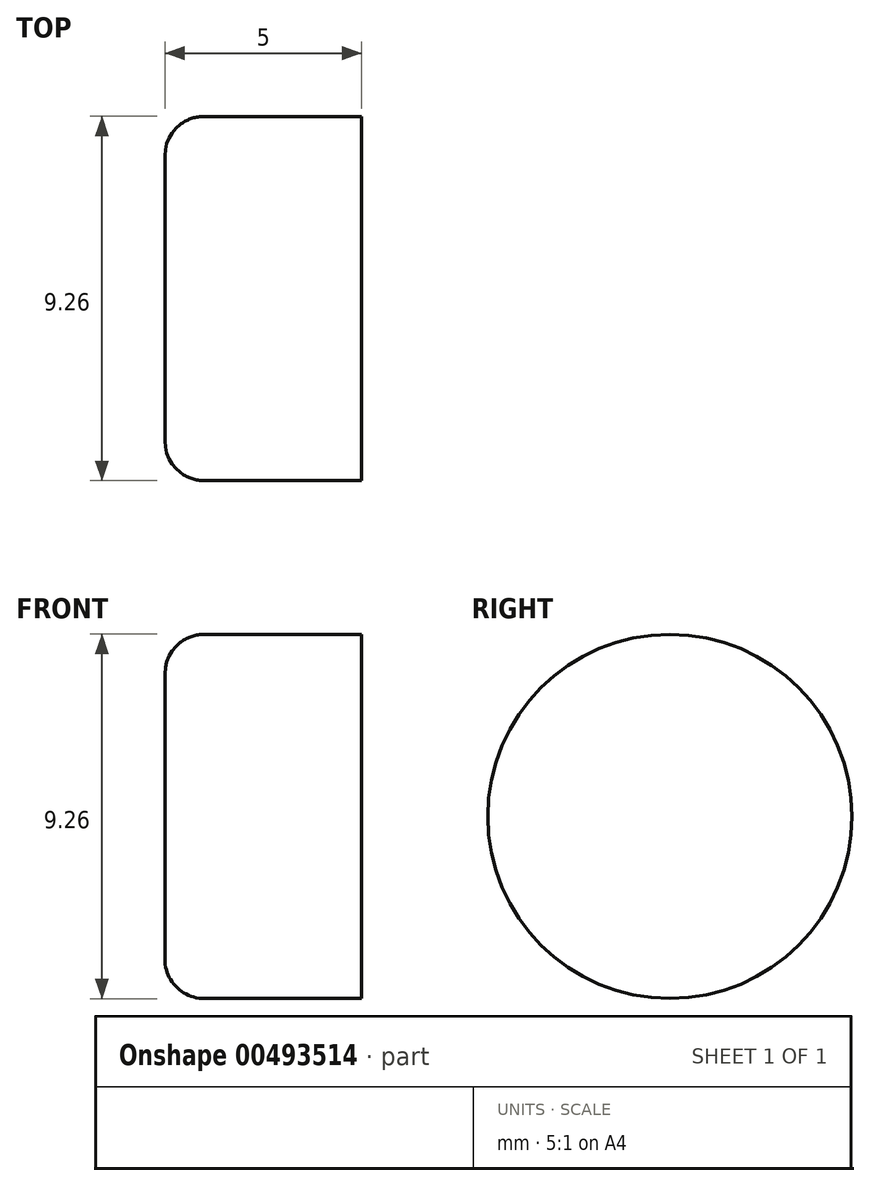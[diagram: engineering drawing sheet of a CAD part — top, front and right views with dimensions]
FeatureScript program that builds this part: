
annotation { "Feature Type Name" : "Feature", "Feature Type Description" : "" }
export const myFeature = defineFeature(function(context is Context, id is Id, definition is map)
    precondition{}
    {
        {
            var Q0;
            Q0=qCreatedBy(makeId("Right.planeOp"),FACE);
            var sketch = newSketch(context, id + "F0", { "sketchPlane" : qUnion([Q0])});
            skCircle(sketch, "E0", {"center": v(0, 0) * mm, "radius": 4.63 * mm});
            skSolve(sketch);
        }
        {
            var Q0;
            Q0 = qSketchRegion(id + "F0", true);
            extrude(context, id + "F1", {"entities" : qUnion([Q0]), "depth" : 5 * mm});
        }
        {
            var Q0;
            Q0=makeQuery(id+"F1.opExtrude","CAP_EDGE",EDGE,{"disambiguationData":[OSD([sQuery(id+"F0.wireOp",EDGE,"E0")])],"isStart":true});
            fillet(context, id + "F2", {"entities" : qUnion([Q0]), "radius" : 1 * mm, "tangentPropagation" : true, "allowEdgeOverflow" : false});
        }
    });
